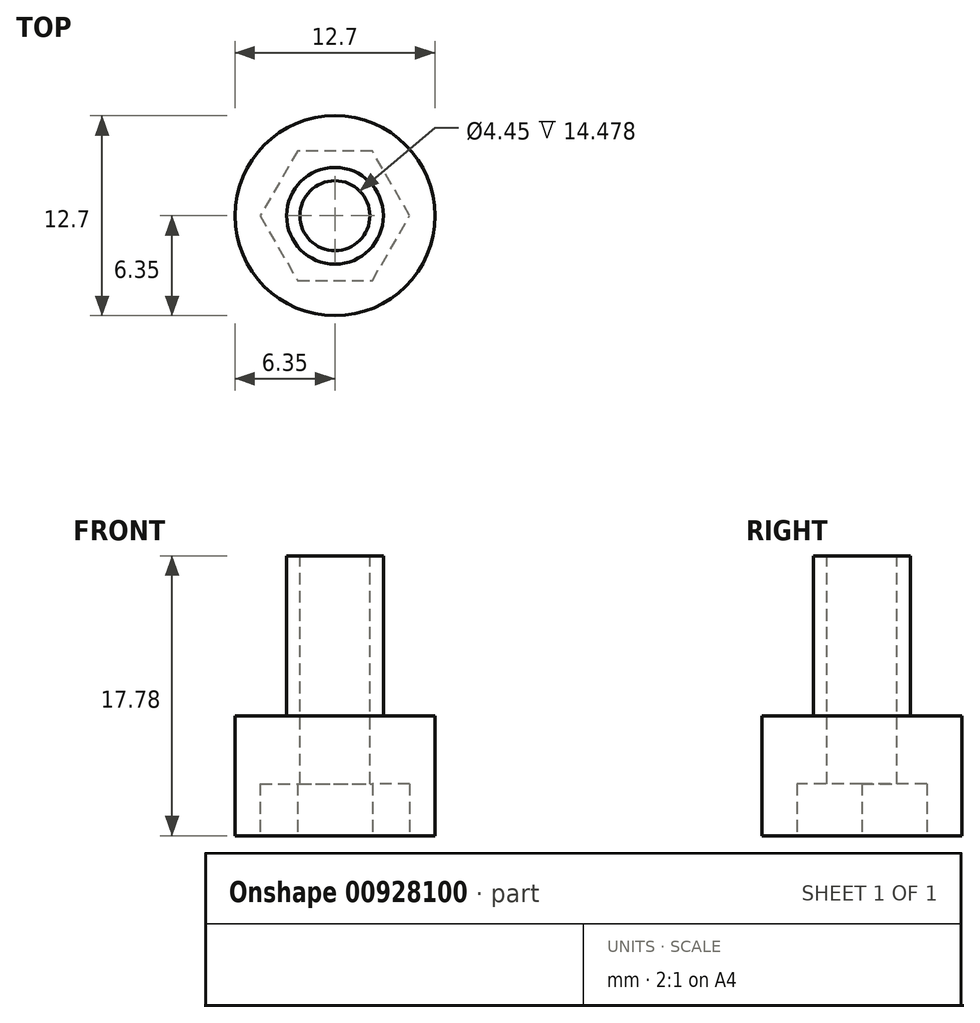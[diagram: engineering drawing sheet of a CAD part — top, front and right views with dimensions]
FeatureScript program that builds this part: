
annotation { "Feature Type Name" : "Feature", "Feature Type Description" : "" }
export const myFeature = defineFeature(function(context is Context, id is Id, definition is map)
    precondition{}
    {
        {
            var Q0;
            Q0=qCreatedBy(makeId("Top.planeOp"),FACE);
            var sketch = newSketch(context, id + "F0", { "sketchPlane" : qUnion([Q0])});
            skCircle(sketch, "E0", {"center": v(0, 0) * mm, "radius": 6.35 * mm});
            skSolve(sketch);
        }
        {
            var Q0;
            Q0=qSketchRegion(id+"F0",true);
            extrude(context, id + "F1", {"entities" : qUnion([Q0]), "depth" : 7.62 * mm, "offsetDistance" : 25.4 * mm});
        }
        {
            var Q0;
            Q0=makeQuery(id+"F1.opExtrude","CAP_FACE",FACE,{"disambiguationData":[OSD([sQuery(id+"F0.wireOp",EDGE,"E0")])],"isStart":false});
            var sketch = newSketch(context, id + "F2", { "sketchPlane" : qUnion([Q0])});
            skCircle(sketch, "E1", {"center": v(0, 0) * mm, "radius": 3.07 * mm});
            skSolve(sketch);
        }
        {
            var Q0;
            Q0=qSketchRegion(id+"F2",true);
            extrude(context, id + "F3", {"entities" : qUnion([Q0]), "operationType" : NewBodyOperationType.ADD, "depth" : 10.16 * mm, "offsetDistance" : 25.4 * mm});
        }
        {
            var Q0;
            Q0=makeQuery(id+"F3.opExtrude","CAP_FACE",FACE,{"disambiguationData":[OSD([sQuery(id+"F2.wireOp",EDGE,"E1")])],"isStart":false});
            var sketch = newSketch(context, id + "F4", { "sketchPlane" : qUnion([Q0])});
            skCircle(sketch, "E2", {"center": v(0, 0) * mm, "radius": 2.22 * mm});
            skSolve(sketch);
        }
        {
            var Q0;
            Q0=qSketchRegion(id+"F4",true);
            extrude(context, id + "F5", {"entities" : qUnion([Q0]), "operationType" : NewBodyOperationType.REMOVE, "endBound" : BoundingType.THROUGH_ALL, "oppositeDirection" : true, "depth" : 25.4 * mm, "offsetDistance" : 25.4 * mm});
        }
        {
            var Q0;
            Q0=makeQuery(id+"F1.opExtrude","CAP_FACE",FACE,{"disambiguationData":[OSD([sQuery(id+"F0.wireOp",EDGE,"E0")])],"isStart":true});
            var sketch = newSketch(context, id + "F6", { "sketchPlane" : qUnion([Q0])});
            skCircle(sketch, "E3.cCircle", {"center": v(0, 0) * mm, "radius": 4.11 * mm, "construction": true});
            skLineSegment(sketch, "E3.0", {"start": v(-2.37, 4.11) * mm, "end": v(2.37, 4.11) * mm});
            skLineSegment(sketch, "E3.1", {"start": v(2.37, 4.11) * mm, "end": v(4.75, 0) * mm});
            skLineSegment(sketch, "E3.2", {"start": v(4.75, 0) * mm, "end": v(2.37, -4.11) * mm});
            skLineSegment(sketch, "E3.3", {"start": v(2.37, -4.11) * mm, "end": v(-2.37, -4.11) * mm});
            skLineSegment(sketch, "E3.4", {"start": v(-2.37, -4.11) * mm, "end": v(-4.75, 0) * mm});
            skLineSegment(sketch, "E3.5", {"start": v(-4.75, 0) * mm, "end": v(-2.37, 4.11) * mm});
            skPoint(sketch, "E3.0.midPoint", {"position": v(0, 4.11) * mm});
            skSolve(sketch);
        }
        {
            var Q0;
            Q0 = qSketchRegion(id + "F6", true);
            extrude(context, id + "F7", {"entities" : qUnion([Q0]), "operationType" : NewBodyOperationType.REMOVE, "oppositeDirection" : true, "depth" : 3.3 * mm, "offsetDistance" : 25.4 * mm});
        }
    });
